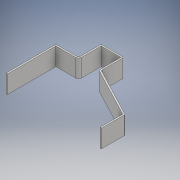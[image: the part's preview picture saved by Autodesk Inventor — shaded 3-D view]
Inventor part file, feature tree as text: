
AUTODESK INVENTOR PART (.ipt)
format: ipt  version: 2018 (Build 220112000, 112)  size: 122,368 bytes
history: native  units: mm
features: other x1, extrude x1, sketch x1
ambient origin geometry x8: Origin, YZ Plane, XZ Plane, XY Plane, X Axis, Y Axis, Z Axis, Center Point
bodies: Body1 (feature_tree)
feature tree (3):
  other  "Sólido1"
  extrude  "Extrusión1"  Depth=75.0mm TaperAngle=0.0deg
  sketch  "Boceto1"  dims[d0=6.0mm d1=75.0mm d2=0.0mm]
